# Revit family: Casement_28_I_Top_Hung_Custom
name_source: partatom
category: Windows
revit_build: Autodesk Revit 2014 (Build: 20130308_1515(x64)
units: mm (PartAtom-declared; Revit-internal decimal feet)

## types (1)
- 28-TypeI-Custom
    Aluminium Thickness = 1 mm  [stored 0.00328084 ft]
    Area Pane Left Bottom = 0.15 m²
    Area Pane Left Middle = 0.23 m²
    Area Pane Left Top = 0.23 m²
    Area Pane Right = 0.8 m²
    Bead SG Gap = 13 mm  [stored 0.0426509 ft]
    Bottom Hung = No
    Casement Dimension = 28 mm  [stored 0.0918635 ft]
    Custom Sash Bottom Height = 554 mm  [stored 1.81759 ft]
    Custom Sash Top Height = 554 mm  [stored 1.81759 ft]
    Custom Sash Width = 554 mm  [stored 1.81759 ft]
    Custom Windload = 1000 mm  [stored 3.28084 ft]
    Custom Window Exterior Offset = 81 mm  [stored 0.265748 ft]
    Custom Window Height = 1500 mm  [stored 4.92126 ft]
    Custom Window Width = 1200 mm  [stored 3.93701 ft]
    Default Sill Height = 800 mm  [stored 2.62467 ft]
    Depth Bead = 14 mm  [stored 0.0459318 ft]
    Depth Mullion = 54 mm  [stored 0.177165 ft]
    Description = Window 28mm, Type I top hung custom
    Frame Center Offset = 14 mm  [stored 0.0459318 ft]
    Height = 1500 mm  [stored 4.92126 ft]
    Height Panel 1 = 540 mm  [stored 1.77165 ft]
    Height Panel 2 = 540 mm  [stored 1.77165 ft]
    Height Panel 3 = 300 mm  [stored 0.984252 ft]
    Height Panel 4 = 1440 mm
    Height Sash Bottom = 524 mm  [stored 1.71916 ft]
    Height Sash Bottom Opening = 554 mm  [stored 1.81759 ft]
    Height Sash Top = 524 mm  [stored 1.71916 ft]
    Height Sash Top Opening = 554 mm  [stored 1.81759 ft]
    Length Mullion = 1500 mm  [stored 4.92126 ft]
    Length Transom = 540 mm  [stored 1.77165 ft]
    Limit Fixed Pane Height Max = 1800 mm  [stored 5.90551 ft]
    Limit Fixed Pane Height Min = 200 mm  [stored 0.656168 ft]
    Limit Fixed Pane Width Max = 1500 mm  [stored 4.92126 ft]
    Limit Fixed Pane Width Min = 200 mm  [stored 0.656168 ft]
    Limit Sash Bottom Height Max = 600 mm  [stored 1.9685 ft]
    Limit Sash Bottom Height Max Based On Top Sash = 654 mm
    Limit Sash Bottom Height Max Calc = 600 mm  [stored 1.9685 ft]
    Limit Sash Bottom Height Min = 300 mm  [stored 0.984252 ft]
    Limit Sash Top Height Max = 600 mm  [stored 1.9685 ft]
    Limit Sash Top Height Min = 300 mm  [stored 0.984252 ft]
    Limit Sash Width Max = 900 mm  [stored 2.95276 ft]
    Limit Sash Width Min = 300 mm  [stored 0.984252 ft]
    Limit Window Height Max = 1860 mm  [stored 6.10236 ft]
    Limit Window Height Min = 1400 mm  [stored 4.59318 ft]
    Limit Window Width Max = 2130 mm  [stored 6.98819 ft]
    Limit Window Width Min = 830 mm  [stored 2.7231 ft]
    Manufacturer = Crealco
    Max Pane Area = 0.8 m²
    Model = Casement 28
    Mullion Depth Windload Based = 54 mm  [stored 0.177165 ft]
    Offset Bead SG Center Reversed = 14 mm  [stored 0.0459318 ft]
    Offset Mullion Left = 570 mm  [stored 1.87008 ft]
    Offset Panel 3 Bead Top = 1170 mm  [stored 3.83858 ft]
    Offset Panel 4 Left = 600 mm  [stored 1.9685 ft]
    Offset Sash 1 Top = 23 mm  [stored 0.0754593 ft]
    Offset Sash 2 Top = 593 mm  [stored 1.94554 ft]
    Offset Sash Left = 23 mm  [stored 0.0754593 ft]
    Offset Transom 1 Top = 570 mm  [stored 1.87008 ft]
    Offset Transom 2 Top = 1140 mm  [stored 3.74016 ft]
    Offset Window Exterior = 95 mm  [stored 0.31168 ft]
    SG Gasket Thickness = 6 mm  [stored 0.019685 ft]
    Sash Center Offset = 11 mm  [stored 0.0360892 ft]
    Sash Overlap = 7 mm  [stored 0.0229659 ft]
    Sash Spacing Inner = 8 mm  [stored 0.0262467 ft]
    Single Glazing = Yes
    Top Hung = Yes
    URL = http://www.crealco.co.za
    Wall Closure = By host
    Width = 1200 mm  [stored 3.93701 ft]
    Width Bead = 15 mm  [stored 0.0492126 ft]
    Width Panel 1 = 540 mm  [stored 1.77165 ft]
    Width Panel 2 = 540 mm  [stored 1.77165 ft]
    Width Panel 3 = 540 mm  [stored 1.77165 ft]
    Width Panel 4 = 570 mm  [stored 1.87008 ft]
    Width Profile = 30 mm  [stored 0.0984252 ft]
    Width Sash 1 = 524 mm  [stored 1.71916 ft]
    Width Sash 2 = 524 mm  [stored 1.71916 ft]
    Width Sash Opening = 554 mm  [stored 1.81759 ft]
    Windload Design = 1000 mm  [stored 3.28084 ft]

note: [stored X ft] marks values corroborated as IEEE doubles in the binary element streams (Revit-internal decimal feet)

## geometry (parser evidence)
native form markers: Blend x4, Sweep x23
no freeform markers — native parametric forms only
